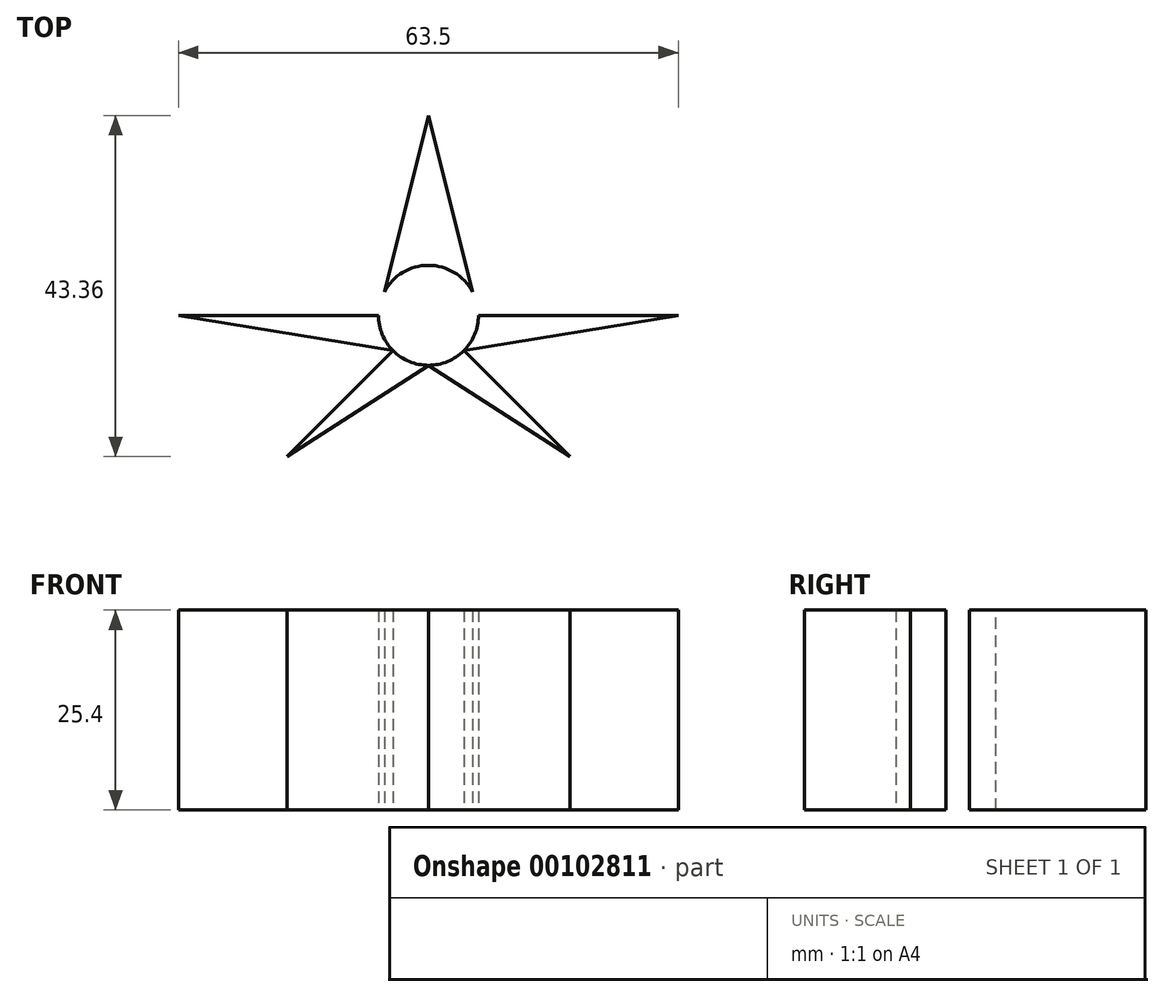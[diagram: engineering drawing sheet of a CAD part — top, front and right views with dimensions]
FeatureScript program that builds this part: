
annotation { "Feature Type Name" : "Feature", "Feature Type Description" : "" }
export const myFeature = defineFeature(function(context is Context, id is Id, definition is map)
    precondition{}
    {
        {
            var Q0;
            Q0=qCreatedBy(makeId("Top.planeOp"),FACE);
            var sketch = newSketch(context, id + "F0", { "sketchPlane" : qUnion([Q0])});
            skCircle(sketch, "E0", {"center": v(0, 0) * mm, "radius": 6.35 * mm});
            skLineSegment(sketch, "E1", {"start": v(6.35, 0) * mm, "end": v(31.75, 0) * mm});
            skLineSegment(sketch, "E2", {"start": v(0, 0) * mm, "end": v(17.96, -17.96) * mm});
            skLineSegment(sketch, "E3", {"start": v(0, 0) * mm, "end": v(-17.96, -17.96) * mm});
            skLineSegment(sketch, "E4", {"start": v(-17.96, -17.96) * mm, "end": v(0, -6.35) * mm});
            skLineSegment(sketch, "E5", {"start": v(0, -6.35) * mm, "end": v(17.96, -17.96) * mm});
            skLineSegment(sketch, "E6", {"start": v(31.75, 0) * mm, "end": v(4.5, -4.5) * mm});
            skLineSegment(sketch, "E7", {"start": v(-6.35, 0) * mm, "end": v(-31.75, 0) * mm});
            skLineSegment(sketch, "E8", {"start": v(-31.75, 0) * mm, "end": v(-4.5, -4.5) * mm});
            skLineSegment(sketch, "E9", {"start": v(0, 0) * mm, "end": v(0, 25.4) * mm});
            skLineSegment(sketch, "E10", {"start": v(-6.35, 0) * mm, "end": v(0, 25.4) * mm});
            skLineSegment(sketch, "E11", {"start": v(6.35, 0) * mm, "end": v(0, 25.4) * mm});
            skSolve(sketch);
        }
        {
            var Q0;
            Q0 = qSketchRegion(id + "F0", true);
            extrude(context, id + "F1", {"entities" : qUnion([Q0]), "depth" : 25.4 * mm});
        }
        {
            var Q0;
            Q0=makeQuery(id+"F1.opExtrude","CAP_FACE",FACE,{"disambiguationData":[OSD([sQuery(id+"F0.wireOp",EDGE,"E0"),sQuery(id+"F0.wireOp",EDGE,"E1"),sQuery(id+"F0.wireOp",EDGE,"E2"),sQuery(id+"F0.wireOp",EDGE,"E3"),sQuery(id+"F0.wireOp",EDGE,"E4"),sQuery(id+"F0.wireOp",EDGE,"E5"),sQuery(id+"F0.wireOp",EDGE,"E6"),sQuery(id+"F0.wireOp",EDGE,"E7"),sQuery(id+"F0.wireOp",EDGE,"E8"),sQuery(id+"F0.wireOp",EDGE,"E10"),sQuery(id+"F0.wireOp",EDGE,"E11")])],"isStart":false});
            var sketch = newSketch(context, id + "F2", { "sketchPlane" : qUnion([Q0])});
            skCircle(sketch, "E12", {"center": v(0, 0) * mm, "radius": 6.35 * mm});
            skSolve(sketch);
        }
        {
            var Q0;
            Q0 = qSketchRegion(id + "F2", true);
            extrude(context, id + "F3", {"entities" : qUnion([Q0]), "operationType" : NewBodyOperationType.REMOVE, "oppositeDirection" : true, "depth" : 25.4 * mm});
        }
    });
